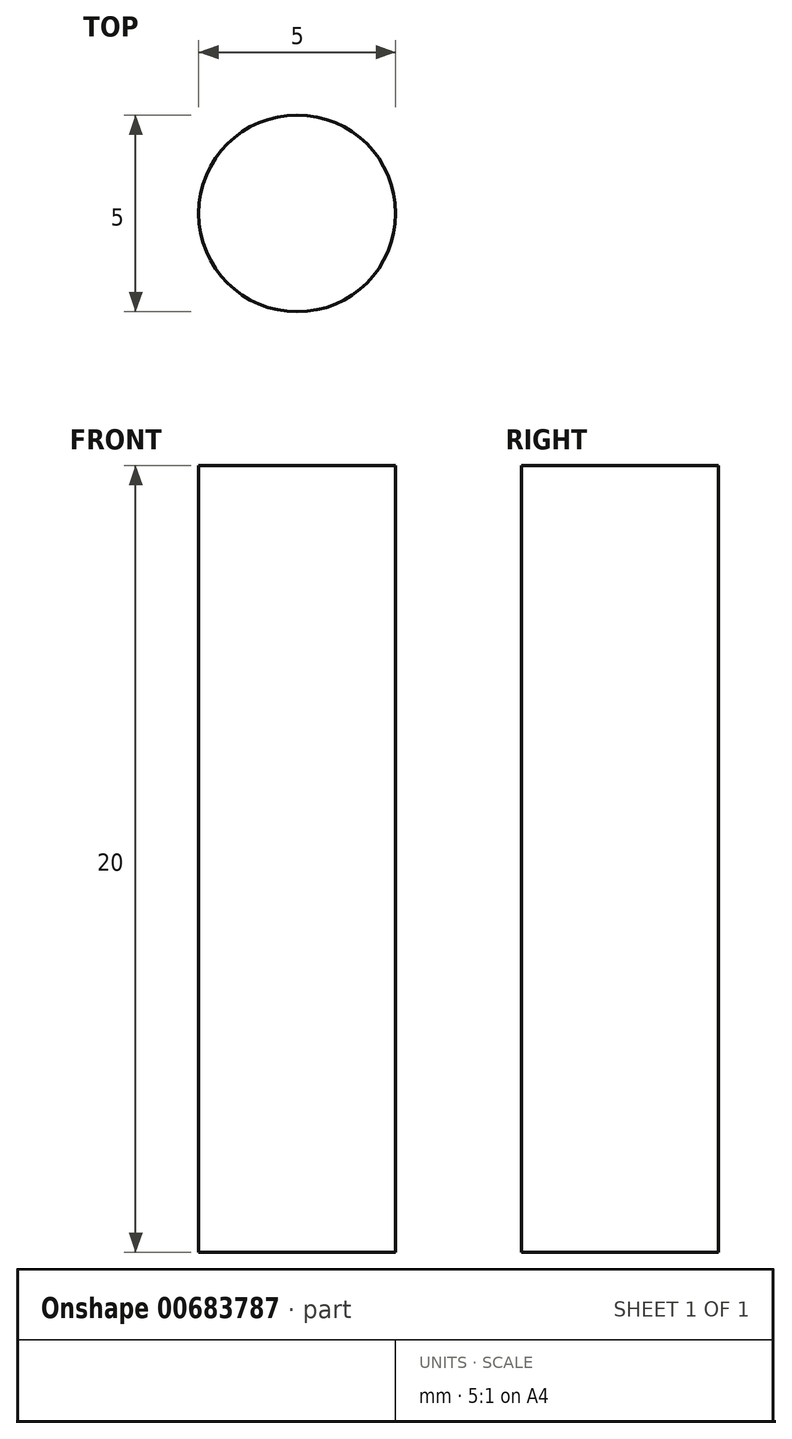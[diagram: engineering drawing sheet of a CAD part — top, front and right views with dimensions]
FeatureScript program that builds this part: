
annotation { "Feature Type Name" : "Feature", "Feature Type Description" : "" }
export const myFeature = defineFeature(function(context is Context, id is Id, definition is map)
    precondition{}
    {
        {
            var Q0;
            Q0=qCreatedBy(makeId("Top.planeOp"),FACE);
            var sketch = newSketch(context, id + "F0", { "sketchPlane" : qUnion([Q0])});
            skCircle(sketch, "E0", {"center": v(0, 0) * mm, "radius": 2.5 * mm});
            skSolve(sketch);
        }
        {
            var Q0;
            Q0=makeQuery(id+"F0.imprint","IMPRINT",FACE,{"disambiguationData":[TD([[makeQuery(id+"F0.imprint","IMPRINT",EDGE,{"derivedFrom":sQuery(id+"F0.wireOp",EDGE,"E0")}),1.0]])]});
            extrude(context, id + "F1", {"entities" : qUnion([Q0]), "endBound" : BoundingType.SYMMETRIC, "depth" : 20 * mm, "offsetDistance" : 25 * mm});
        }
    });
